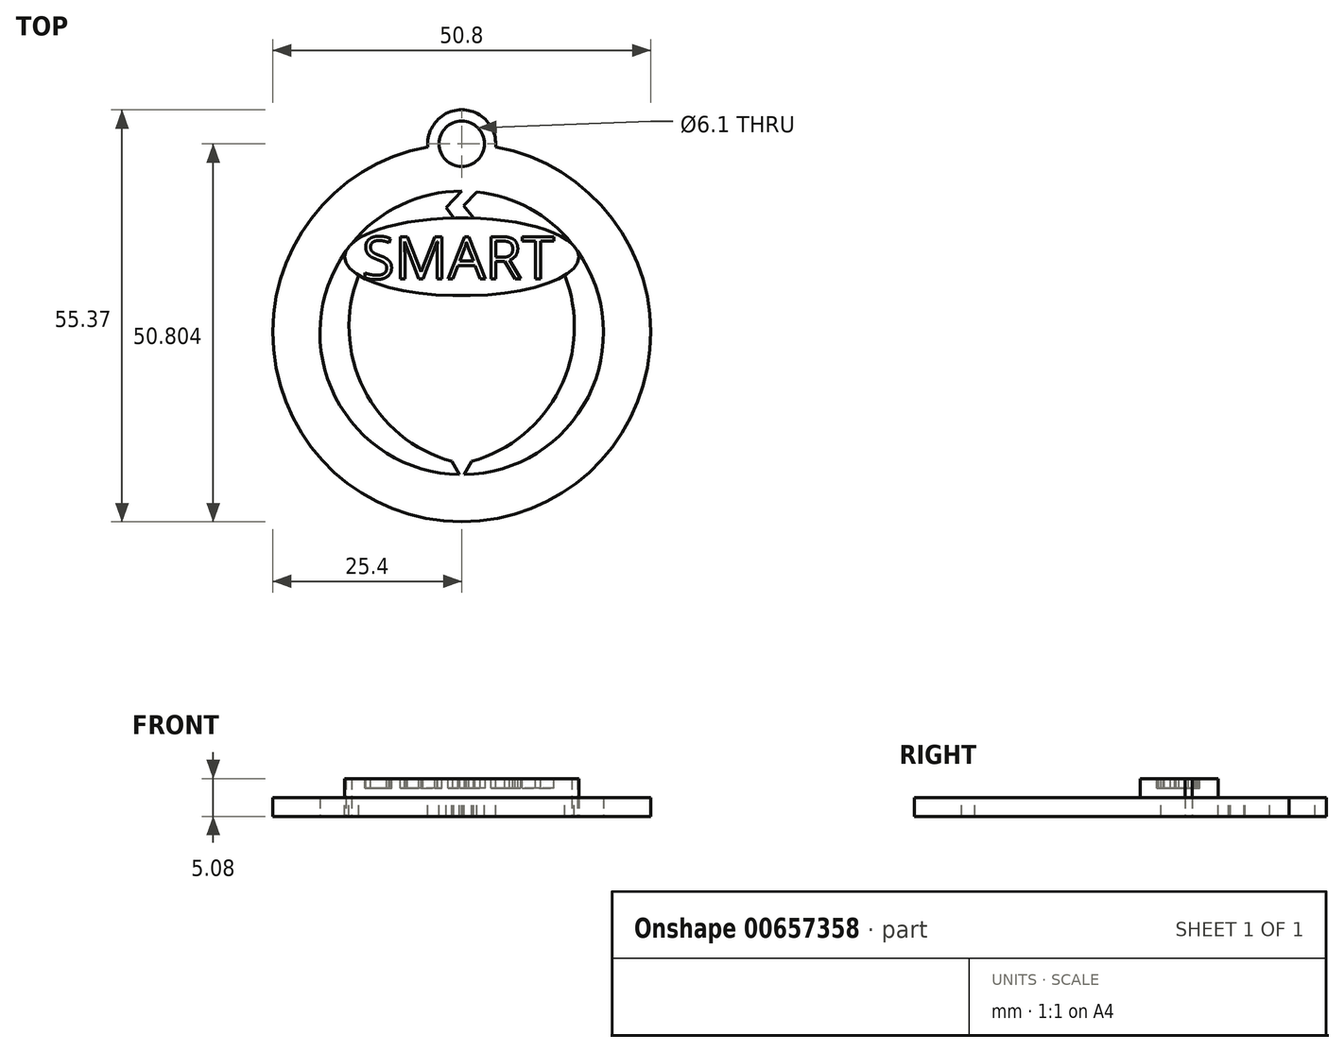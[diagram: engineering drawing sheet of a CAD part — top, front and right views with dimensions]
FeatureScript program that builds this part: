
annotation { "Feature Type Name" : "Feature", "Feature Type Description" : "" }
export const myFeature = defineFeature(function(context is Context, id is Id, definition is map)
    precondition{}
    {
        {
            var Q0;
            Q0=qCreatedBy(makeId("Top.planeOp"),FACE);
            var sketch = newSketch(context, id + "F0", { "sketchPlane" : qUnion([Q0])});
            skCircle(sketch, "E0", {"center": v(0, 0) * mm, "radius": 25.4 * mm});
            skCircle(sketch, "E1", {"center": v(0, 0) * mm, "radius": 19.05 * mm});
            skSolve(sketch);
        }
        {
            var Q0;
            Q0=makeQuery(id+"F0.imprint","IMPRINT",FACE,{"disambiguationData":[TD([[makeQuery(id+"F0.imprint","IMPRINT",EDGE,{"derivedFrom":sQuery(id+"F0.wireOp",EDGE,"E0")}),1.0]])]});
            extrude(context, id + "F1", {"entities" : qUnion([Q0]), "depth" : 2.54 * mm, "offsetDistance" : 25.4 * mm});
        }
        {
            var Q0;
            Q0=makeQuery(id+"F1.opExtrude","CAP_FACE",FACE,{"disambiguationData":[OSD([sQuery(id+"F0.wireOp",EDGE,"E0"),sQuery(id+"F0.wireOp",EDGE,"E1")])],"isStart":false});
            var sketch = newSketch(context, id + "F2", { "sketchPlane" : qUnion([Q0])});
            skEllipse(sketch, "E2", {"center": v(0, 10.22) * mm, "majorRadius": 15.73 * mm, "minorRadius": 5.23 * mm, "majorAxis": v(1, 0)});
            skLineSegment(sketch, "E3", {"start": v(1.6, 15.42) * mm, "end": v(0.28, 17.13) * mm});
            skLineSegment(sketch, "E4", {"start": v(0.28, 17.13) * mm, "end": v(2.05, 18.94) * mm});
            skLineSegment(sketch, "E5", {"start": v(-1.06, 15.43) * mm, "end": v(-2.08, 16.82) * mm});
            skLineSegment(sketch, "E6", {"start": v(-2.08, 16.82) * mm, "end": v(0, 19.05) * mm});
            skArc(sketch, "E7", {"start": v(-13.84, 7.73) * mm, "mid": v(-13.16, -7.54) * mm, "end": v(-1.36, -17.26) * mm});
            skLineSegment(sketch, "E8", {"start": v(0, 10.22) * mm, "end": v(0, -27.38) * mm, "construction": true});
            skArc(sketch, "E9.MirrorCS", {"start": v(13.84, 7.73) * mm, "mid": v(13.16, -7.54) * mm, "end": v(1.36, -17.26) * mm});
            skLineSegment(sketch, "E10", {"start": v(-1.36, -17.26) * mm, "end": v(0, -19.58) * mm});
            skLineSegment(sketch, "E11", {"start": v(0, -19.58) * mm, "end": v(1.36, -17.26) * mm});
            skSolve(sketch);
        }
        {
            var Q0;
            {var subQ2=sQuery(id+"F2.wireOp",EDGE,"E3");Q0=makeQuery(id+"F2.imprint","IMPRINT",FACE,{"disambiguationData":[TD([[makeQuery(id+"F2.imprint","IMPRINT",EDGE,{"derivedFrom":subQ2}),1.0]])]});}
            var Q1;
            {var subQ1=sQuery(id+"F2.wireOp",EDGE,"E7");Q1=makeQuery(id+"F2.imprint","IMPRINT",FACE,{"disambiguationData":[TD([[makeQuery(id+"F2.imprint","IMPRINT",EDGE,{"derivedFrom":subQ1}),1.0]])]});}
            extrude(context, id + "F3", {"entities" : qUnion([Q0, Q1]), "operationType" : NewBodyOperationType.ADD, "oppositeDirection" : true, "depth" : 2.54 * mm, "offsetDistance" : 25.4 * mm});
        }
        {
            var Q0;
            {var subQ0=sQuery(id+"F2.wireOp",EDGE,"E2");var subQ6=makeQuery(id+"F2.imprint","INTERSECT",VERTEX,{"derivedFrom":[subQ0,sQuery(id+"F2.wireOp",EDGE,"E3")]});Q0=makeQuery(id+"F2.imprint","IMPRINT",FACE,{"disambiguationData":[TD([[makeQuery(id+"F2.imprint","IMPRINT",EDGE,{"disambiguationData":[TD([[subQ6,1.0]])],"derivedFrom":subQ0}),1.0]])]});}
            extrude(context, id + "F4", {"entities" : qUnion([Q0]), "operationType" : NewBodyOperationType.ADD, "depth" : 2.54 * mm, "offsetDistance" : 25.4 * mm, "hasSecondDirection" : true, "secondDirectionOppositeDirection" : true, "secondDirectionDepth" : 2.54 * mm});
        }
        {
            var Q0;
            Q0=makeQuery(id+"F4.opExtrude","CAP_FACE",FACE,{"disambiguationData":[OSD([sQuery(id+"F0.wireOp",EDGE,"E1"),sQuery(id+"F2.wireOp",EDGE,"E2")])],"isStart":false});
            var sketch = newSketch(context, id + "F5", { "sketchPlane" : qUnion([Q0])});
            skText(sketch, "E12", { "text": "SMART", "fontName": "OpenSans-Regular.ttf"});
            const initialGuessF5  = {"E12": [-0.0134, 0.00724, 1, 0, 0.00572]};
            skSetInitialGuess(sketch, initialGuessF5);
            skSolve(sketch);
        }
        {
            var Q0;
            Q0 = qSketchRegion(id + "F5", true);
            extrude(context, id + "F6", {"entities" : qUnion([Q0]), "operationType" : NewBodyOperationType.REMOVE, "oppositeDirection" : true, "depth" : 1.27 * mm, "offsetDistance" : 25.4 * mm});
        }
        {
            var Q0;
            Q0=makeQuery(id+"F2.imprint","IMPRINT",FACE,{"disambiguationData":[TD([[makeQuery(id+"F2.imprint","IMPRINT",EDGE,{"derivedFrom":makeQuery(id+"F1.opExtrude","CAP_EDGE",EDGE,{"disambiguationData":[OSD([sQuery(id+"F0.wireOp",EDGE,"E0")])],"isStart":false})}),1.0]])]});
            var sketch = newSketch(context, id + "F7", { "sketchPlane" : qUnion([Q0])});
            skCircle(sketch, "E13", {"center": v(0, 25.4) * mm, "radius": 4.57 * mm});
            skSolve(sketch);
        }
        {
            var Q0;
            Q0 = qSketchRegion(id + "F7", true);
            extrude(context, id + "F8", {"entities" : qUnion([Q0]), "operationType" : NewBodyOperationType.ADD, "oppositeDirection" : true, "depth" : 2.54 * mm, "offsetDistance" : 25.4 * mm});
        }
        {
            var Q0;
            Q0=makeQuery(id+"F2.imprint","IMPRINT",FACE,{"disambiguationData":[TD([[makeQuery(id+"F2.imprint","IMPRINT",EDGE,{"derivedFrom":makeQuery(id+"F1.opExtrude","CAP_EDGE",EDGE,{"disambiguationData":[OSD([sQuery(id+"F0.wireOp",EDGE,"E0")])],"isStart":false})}),1.0]])]});
            var sketch = newSketch(context, id + "F9", { "sketchPlane" : qUnion([Q0])});
            skCircle(sketch, "E14", {"center": v(0, 25.4) * mm, "radius": 3.05 * mm});
            skSolve(sketch);
        }
        {
            var Q0;
            {var subQ0=sQuery(id+"F9.wireOp",EDGE,"E14");var subQ1=makeQuery(id+"F2.imprint","IMPRINT",EDGE,{"derivedFrom":makeQuery(id+"F1.opExtrude","CAP_EDGE",EDGE,{"disambiguationData":[OSD([sQuery(id+"F0.wireOp",EDGE,"E0")])],"isStart":false})});var subQ2=makeQuery(id+"F9.imprint","INTERSECT",VERTEX,{"disambiguationData":[OD(0.0)],"derivedFrom":[subQ1,subQ0]});Q0=makeQuery(id+"F9.imprint","IMPRINT",FACE,{"disambiguationData":[TD([[makeQuery(id+"F9.imprint","IMPRINT",EDGE,{"disambiguationData":[TD([[subQ2,1.0]])],"derivedFrom":subQ0}),1.0]])]});}
            var Q1;
            {var subQ0=sQuery(id+"F9.wireOp",EDGE,"E14");var subQ1=makeQuery(id+"F2.imprint","IMPRINT",EDGE,{"derivedFrom":makeQuery(id+"F1.opExtrude","CAP_EDGE",EDGE,{"disambiguationData":[OSD([sQuery(id+"F0.wireOp",EDGE,"E0")])],"isStart":false})});var subQ2=makeQuery(id+"F9.imprint","INTERSECT",VERTEX,{"disambiguationData":[OD(0.0)],"derivedFrom":[subQ1,subQ0]});Q1=makeQuery(id+"F9.imprint","IMPRINT",FACE,{"disambiguationData":[TD([[makeQuery(id+"F9.imprint","IMPRINT",EDGE,{"disambiguationData":[TD([[subQ2,-1.0]])],"derivedFrom":subQ0}),1.0]])]});}
            extrude(context, id + "F10", {"entities" : qUnion([Q0, Q1]), "operationType" : NewBodyOperationType.REMOVE, "oppositeDirection" : true, "depth" : 25.4 * mm, "offsetDistance" : 25.4 * mm});
        }
    });
